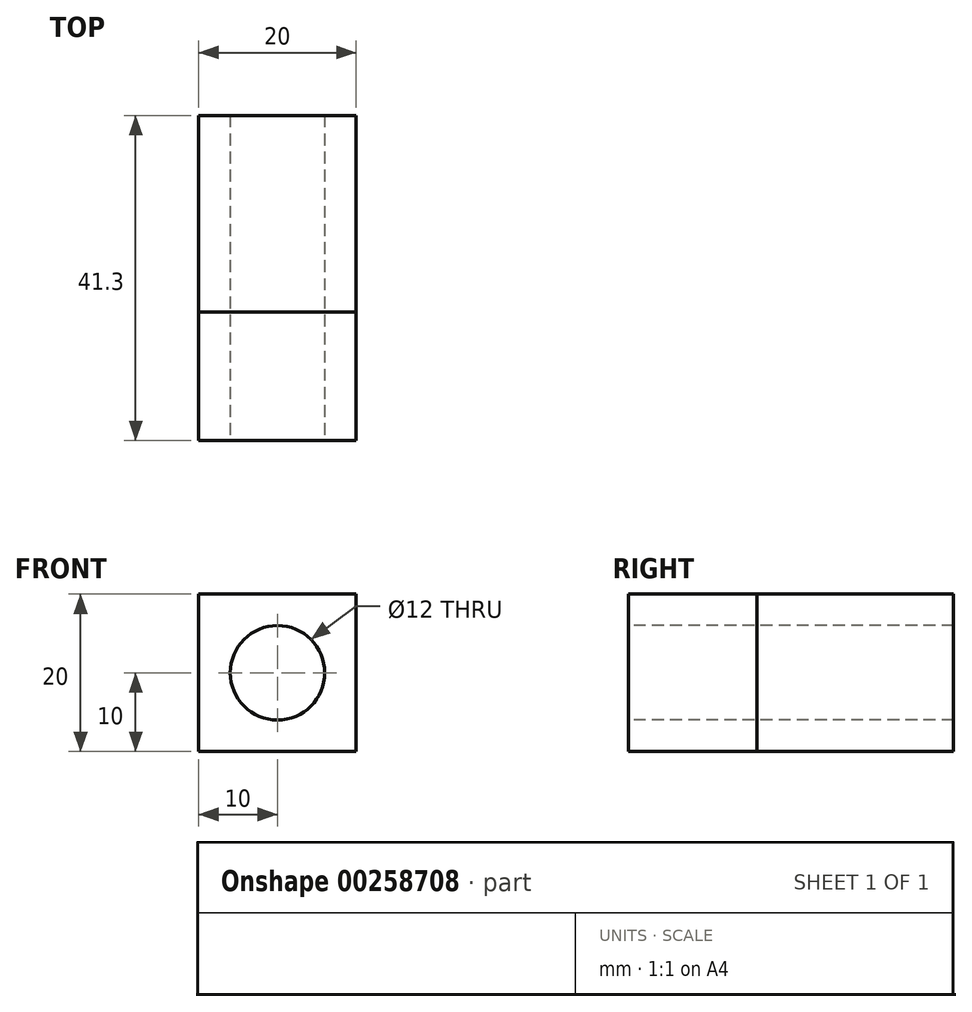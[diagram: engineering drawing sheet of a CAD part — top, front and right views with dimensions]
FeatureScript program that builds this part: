
annotation { "Feature Type Name" : "Feature", "Feature Type Description" : "" }
export const myFeature = defineFeature(function(context is Context, id is Id, definition is map)
    precondition{}
    {
        {
            var Q0;
            Q0=qCreatedBy(makeId("Front.planeOp"),FACE);
            var sketch = newSketch(context, id + "F0", { "sketchPlane" : qUnion([Q0])});
            skLineSegment(sketch, "E0.bottom", {"start": v(-10, 10) * mm, "end": v(10, 10) * mm});
            skLineSegment(sketch, "E0.top", {"start": v(-10, -10) * mm, "end": v(10, -10) * mm});
            skLineSegment(sketch, "E0.left", {"start": v(-10, 10) * mm, "end": v(-10, -10) * mm});
            skLineSegment(sketch, "E0.right", {"start": v(10, 10) * mm, "end": v(10, -10) * mm});
            skPoint(sketch, "E0.middle", {"position": v(0, 0) * mm});
            skSolve(sketch);
        }
        {
            var Q0;
            Q0 = qSketchRegion(id + "F0", true);
            extrude(context, id + "F1", {"entities" : qUnion([Q0]), "depth" : 41.3 * mm});
        }
        {
            var Q0;
            Q0=makeQuery(id+"F1.opExtrude","CAP_FACE",FACE,{"disambiguationData":[OSD([sQuery(id+"F0.wireOp",EDGE,"E0.bottom"),sQuery(id+"F0.wireOp",EDGE,"E0.top"),sQuery(id+"F0.wireOp",EDGE,"E0.left"),sQuery(id+"F0.wireOp",EDGE,"E0.right")])],"isStart":false});
            var sketch = newSketch(context, id + "F2", { "sketchPlane" : qUnion([Q0])});
            skCircle(sketch, "E1", {"center": v(0, 0) * mm, "radius": 6 * mm});
            skSolve(sketch);
        }
        {
            var Q0;
            Q0=makeQuery(id+"F2.imprint","IMPRINT",FACE,{"disambiguationData":[TD([[makeQuery(id+"F2.imprint","IMPRINT",EDGE,{"derivedFrom":sQuery(id+"F2.wireOp",EDGE,"E1")}),1.0]])]});
            var Q1;
            Q1=sQuery(id+"F2.wireOp",EDGE,"E1");
            extrude(context, id + "F3", {"entities" : qUnion([Q0]), "operationType" : NewBodyOperationType.REMOVE, "surfaceEntities" : qUnion([Q1]), "endBound" : BoundingType.THROUGH_ALL, "oppositeDirection" : true, "depth" : 25 * mm});
        }
        {
            var Q0;
            Q0=makeQuery(id+"F0.imprint","IMPRINT",FACE,{"disambiguationData":[TD([[makeQuery(id+"F0.imprint","IMPRINT",EDGE,{"derivedFrom":sQuery(id+"F0.wireOp",EDGE,"E0.bottom")}),-1.0]])]});
            extrude(context, id + "F4", {"entities" : qUnion([Q0]), "depth" : 25 * mm});
        }
    });
